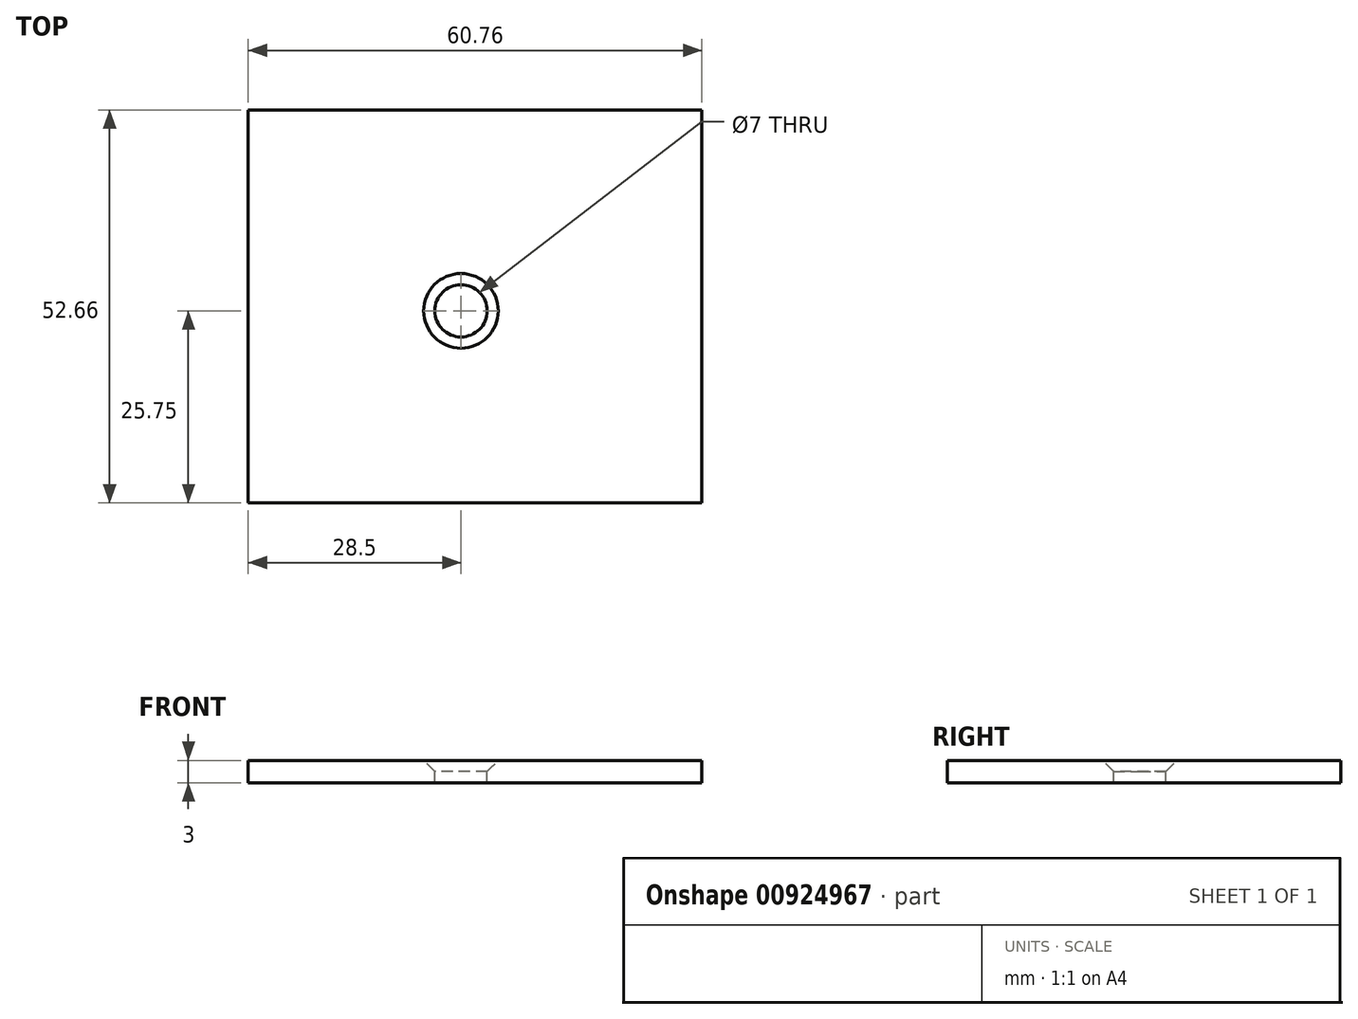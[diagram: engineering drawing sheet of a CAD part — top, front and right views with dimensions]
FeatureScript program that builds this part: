
annotation { "Feature Type Name" : "Feature", "Feature Type Description" : "" }
export const myFeature = defineFeature(function(context is Context, id is Id, definition is map)
    precondition{}
    {
        {
            var Q0;
            Q0=qCreatedBy(makeId("Top.planeOp"),FACE);
            var sketch = newSketch(context, id + "F0", { "sketchPlane" : qUnion([Q0])});
            skLineSegment(sketch, "E0", {"start": v(0, 0) * mm, "end": v(32.26, 0) * mm});
            skLineSegment(sketch, "E1", {"start": v(32.26, 0) * mm, "end": v(32.26, 26.91) * mm});
            skLineSegment(sketch, "E2", {"start": v(32.26, 26.91) * mm, "end": v(0, 26.91) * mm});
            skLineSegment(sketch, "E3", {"start": v(0, 26.91) * mm, "end": v(-28.5, 26.91) * mm});
            skLineSegment(sketch, "E4", {"start": v(-28.5, 26.91) * mm, "end": v(-28.5, 0) * mm});
            skLineSegment(sketch, "E5", {"start": v(-28.5, 0) * mm, "end": v(-28.5, -25.75) * mm});
            skLineSegment(sketch, "E6", {"start": v(-28.5, -25.75) * mm, "end": v(0, -25.75) * mm});
            skLineSegment(sketch, "E7", {"start": v(0, -25.75) * mm, "end": v(32.26, -25.75) * mm});
            skLineSegment(sketch, "E8", {"start": v(32.26, -25.75) * mm, "end": v(32.26, 0) * mm});
            skSolve(sketch);
        }
        {
            var Q0;
            Q0 = qSketchRegion(id + "F0", true);
            extrude(context, id + "F1", {"entities" : qUnion([Q0]), "depth" : 3 * mm, "offsetDistance" : 25.4 * mm});
        }
        {
            var Q0;
            Q0=makeQuery(id+"F1.opExtrude","CAP_FACE",FACE,{"disambiguationData":[OSD([sQuery(id+"F0.wireOp",EDGE,"E1"),sQuery(id+"F0.wireOp",EDGE,"E2"),sQuery(id+"F0.wireOp",EDGE,"E3"),sQuery(id+"F0.wireOp",EDGE,"E4"),sQuery(id+"F0.wireOp",EDGE,"E5"),sQuery(id+"F0.wireOp",EDGE,"E6"),sQuery(id+"F0.wireOp",EDGE,"E7"),sQuery(id+"F0.wireOp",EDGE,"E8")])],"isStart":false});
            var sketch = newSketch(context, id + "F2", { "sketchPlane" : qUnion([Q0])});
            skLineSegment(sketch, "E9", {"start": v(32.26, 0) * mm, "end": v(0, 0) * mm});
            skSolve(sketch);
        }
        {
            var Q0;
            Q0=sQuery(id+"F2.wireOp",VERTEX,"E9.end");
            var Q1;
            Q1=makeQuery(id+"F1.opExtrude","SWEPT_BODY",BODY,{"disambiguationData":[OSD([sQuery(id+"F0.wireOp",EDGE,"E1"),sQuery(id+"F0.wireOp",EDGE,"E2"),sQuery(id+"F0.wireOp",EDGE,"E3"),sQuery(id+"F0.wireOp",EDGE,"E4"),sQuery(id+"F0.wireOp",EDGE,"E5"),sQuery(id+"F0.wireOp",EDGE,"E6"),sQuery(id+"F0.wireOp",EDGE,"E7"),sQuery(id+"F0.wireOp",EDGE,"E8")])]});
            hole(context, id + "F3", {"style" : HoleStyle.C_SINK, "endStyle" : HoleEndStyle.BLIND, "holeDiameter" : 7 * mm, "cSinkDiameter" : 10 * mm, "cSinkAngle" : 90 * degree, "majorDiameter" : 6.35 * mm, "holeDepth" : 15.24 * mm, "isTappedThrough" : true, "tappedDepth" : 12.7 * mm, "tapClearance" : 3, "startFromSketch" : true, "locations" : qUnion([Q0]), "scope" : qUnion([Q1])});
        }
    });
